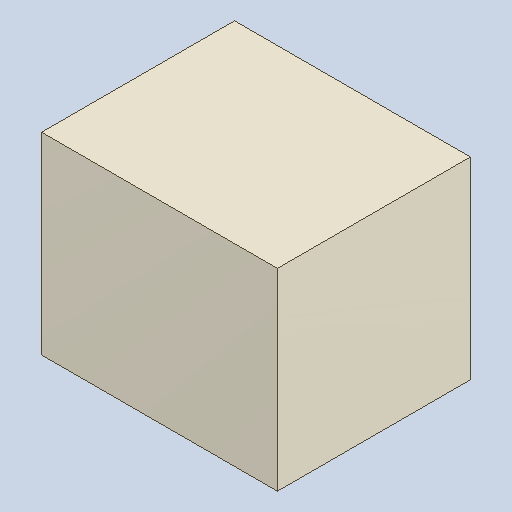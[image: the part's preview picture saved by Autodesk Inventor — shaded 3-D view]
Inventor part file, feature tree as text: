
AUTODESK INVENTOR PART (.ipt)
format: ipt  version: 2023.4 (Build 274418000, 418)  size: 81,920 bytes
history: native  units: mm
features: extrude x1
ambient origin geometry x8: Origin, YZ Plane, XZ Plane, XY Plane, X Axis, Y Axis, Z Axis, Center Point
bodies: Solid1 (feature_tree)
feature tree (1):
  extrude  "Extruded_20"  [1 undecoded]
note: 1 required parameter value undecoded (feature->parameter linkage not recoverable at this tier; creation-order binding heuristic only, values carry confidence <= 0.55)
